# Revit family: 3097176 Lighting Fixture_Sylvania_Insaver LED 75 - Round - White Bezel_Ceiling Recessed
name_source: partatom
category: Lighting Fixtures
revit_build: Autodesk Revit 2017 (Build: 20190507_1515(x64)
units: mm (PartAtom-declared; Revit-internal decimal feet)

## family parameters
Cut with Voids When Loaded = No
Host = Face
Light Source = Yes
OmniClass Number = 23.80.70.11.17
OmniClass Title = Specialized Lighting by Location or Use
Part Type = Normal
Room Calculation Point = No
Round Connector Dimension = Use Diameter
Shared = No

## types (1)
- Insaver 75 LED RS 16W WW EB WH
    Accesory Material = Metallic Paint_Sylvania_Insaver LED 75_White_RAL 9016
    Apparent Load = 16 VA
    Assembly Code = D5020200
    Beam Angle = 55°
    CRI ( Ra ) = 85
    Catalog Number = 3097176 Insaver 75 LED RS 16W WW EB WH
    Color Filter = 16777215
    Cutout Diameter = 75 mm
    Default Elevation = 0 mm  [stored 0 ft]
    Description = Innovative square or round design using array chip technology High colour
rendering index CRI Thermal management ensures service life up to 50.000
hrs Low power consumption - 16W
    Diameter = 90 mm  [stored 0.295276 ft]
    Dimming Lamp Color Temperature Shift = <None>
    Drive Current = 350 mA
    Electrical Protection = Class II
    Emit Shape Visible in Rendering = No
    Emit from Circle Diameter = 50 mm
    Height = 65 mm  [stored 0.213255 ft]
    IP Rating = IP65
    Lamp = 16W High Brightnes LED array
    Lamp Comments = Integrated LED
    Life = 50 000 h
    Manufacturer = Feilo Sylvania
    Model = Insaver 75 LED RS 16W WW EB WH
    Photometric Web File = 3097176_InsaverLED7513WWWSTD-98563.ies
    Product Family = Insaver LED 75 - Round - White Bezel
    Product Page URL = http://www.sylvania-lighting.com
    Radius = 45 mm  [stored 0.147638 ft]
    Reflector Material = Aluminium_Sylvania_Insaver LED 75_Silver
    T Class Max = -1 °C
    T Class Min = -1 °C
    Tilt Angle = -90°
    Transformator Marerial = Metallic Paint_Sylvania_Insaver LED 75_Black_RAL 9005
    URL = http://www.sylvania-lighting.com
    Voltage = 230 V
    Voltage Comments = UNV (Universal Voltage; 230/240 Volt)
    Weight = 0 kg

note: [stored X ft] marks values corroborated as IEEE doubles in the binary element streams (Revit-internal decimal feet)

## geometry (parser evidence)
native form markers: Blend x4, Sweep x1
no freeform markers — native parametric forms only
